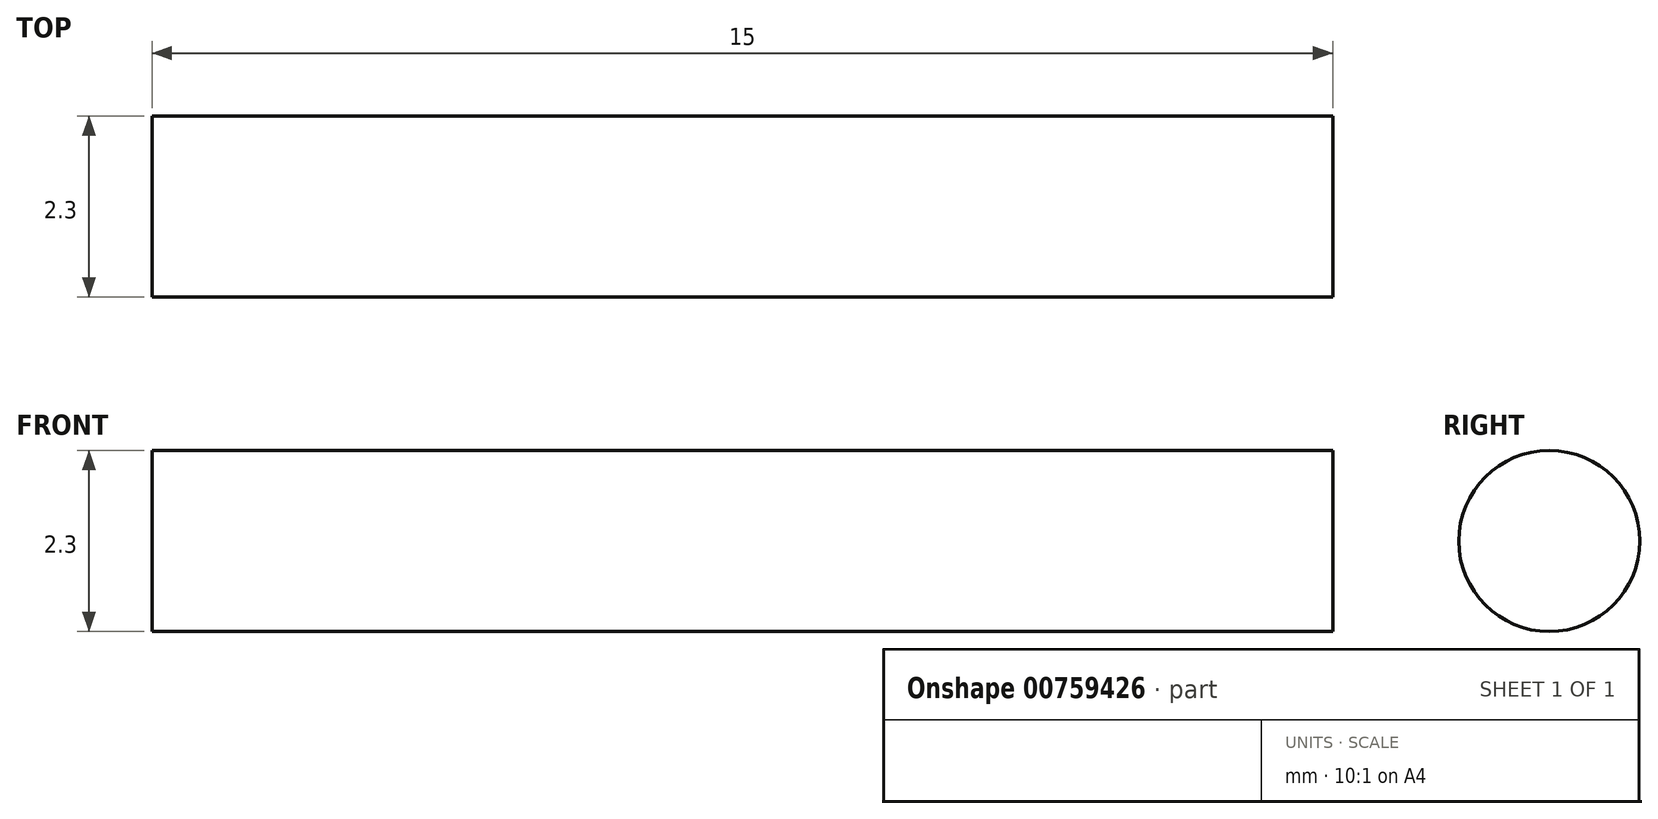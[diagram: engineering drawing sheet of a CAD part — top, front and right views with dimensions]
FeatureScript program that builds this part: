
annotation { "Feature Type Name" : "Feature", "Feature Type Description" : "" }
export const myFeature = defineFeature(function(context is Context, id is Id, definition is map)
    precondition{}
    {
        {
            var Q0;
            Q0=qCreatedBy(makeId("Right.planeOp"),FACE);
            var sketch = newSketch(context, id + "F0", { "sketchPlane" : qUnion([Q0])});
            skCircle(sketch, "E0", {"center": v(0, 0) * mm, "radius": 1.15 * mm});
            skSolve(sketch);
        }
        {
            var Q0;
            Q0 = qSketchRegion(id + "F0", true);
            extrude(context, id + "F1", {"entities" : qUnion([Q0]), "endBound" : BoundingType.SYMMETRIC, "depth" : 15 * mm, "offsetDistance" : 25 * mm});
        }
    });
